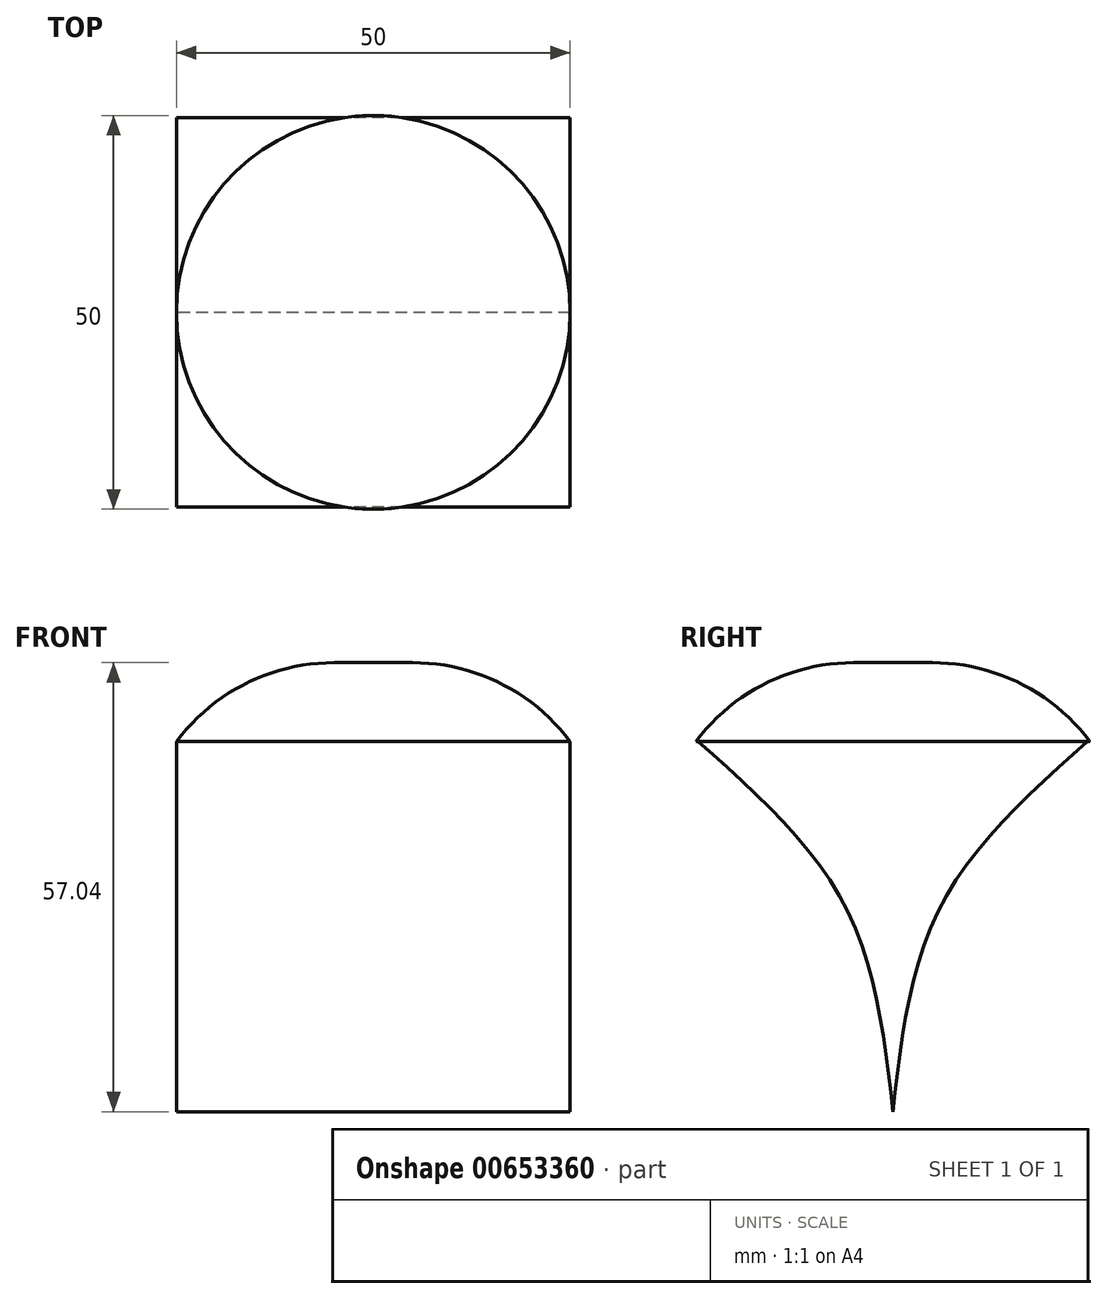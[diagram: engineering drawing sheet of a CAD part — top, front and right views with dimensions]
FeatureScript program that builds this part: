
annotation { "Feature Type Name" : "Feature", "Feature Type Description" : "" }
export const myFeature = defineFeature(function(context is Context, id is Id, definition is map)
    precondition{}
    {
        {
            var Q0;
            Q0=qCreatedBy(makeId("Top.planeOp"),FACE);
            var sketch = newSketch(context, id + "F0", { "sketchPlane" : qUnion([Q0])});
            skCircle(sketch, "E0", {"center": v(0, 0) * mm, "radius": 25 * mm});
            skSolve(sketch);
        }
        {
            var Q0;
            Q0 = qSketchRegion(id + "F0", true);
            extrude(context, id + "F1", {"entities" : qUnion([Q0]), "depth" : 10 * mm, "offsetDistance" : 25 * mm});
        }
        {
            var Q0;
            Q0=makeQuery(id+"F1.opExtrude","CAP_EDGE",EDGE,{"disambiguationData":[OSD([sQuery(id+"F0.wireOp",EDGE,"E0")])],"isStart":false});
            fillet(context, id + "F2", {"entities" : qUnion([Q0]), "radius" : 25 * mm, "tangentPropagation" : true, "allowEdgeOverflow" : false});
        }
        {
            var Q0;
            Q0=qCreatedBy(makeId("Right.planeOp"),FACE);
            var sketch = newSketch(context, id + "F3", { "sketchPlane" : qUnion([Q0])});
            skFitSpline(sketch, "E1", {"points": [v(24.73, 0) * mm, v(6.1, -20.85) * mm, v(0, -47.04) * mm], "startDerivative": vector(-43.08, -38.38) * mm, "endDerivative": vector(-6.26, -55.75) * mm});
            skFitSpline(sketch, "E2.MirrorCS", {"points": [v(-24.73, 0) * mm, v(-6.1, -20.85) * mm, v(0, -47.04) * mm], "startDerivative": vector(43.08, -38.38) * mm, "endDerivative": vector(6.26, -55.75) * mm});
            skLineSegment(sketch, "E3", {"start": v(24.73, 0) * mm, "end": v(-24.73, 0) * mm});
            skSolve(sketch);
        }
        {
            var Q0;
            Q0 = qSketchRegion(id + "F3", true);
            extrude(context, id + "F4", {"entities" : qUnion([Q0]), "operationType" : NewBodyOperationType.ADD, "depth" : 25 * mm, "offsetDistance" : 25 * mm});
        }
        {
            var Q0;
            Q0=makeQuery(id+"F4.opExtrude","CAP_FACE",FACE,{"disambiguationData":[OSD([sQuery(id+"F3.wireOp",EDGE,"E1"),sQuery(id+"F3.wireOp",EDGE,"E2.MirrorCS"),sQuery(id+"F3.wireOp",EDGE,"E3")])],"isStart":true});
            extrude(context, id + "F5", {"entities" : qUnion([Q0]), "operationType" : NewBodyOperationType.ADD, "depth" : 25 * mm, "offsetDistance" : 25 * mm});
        }
    });
